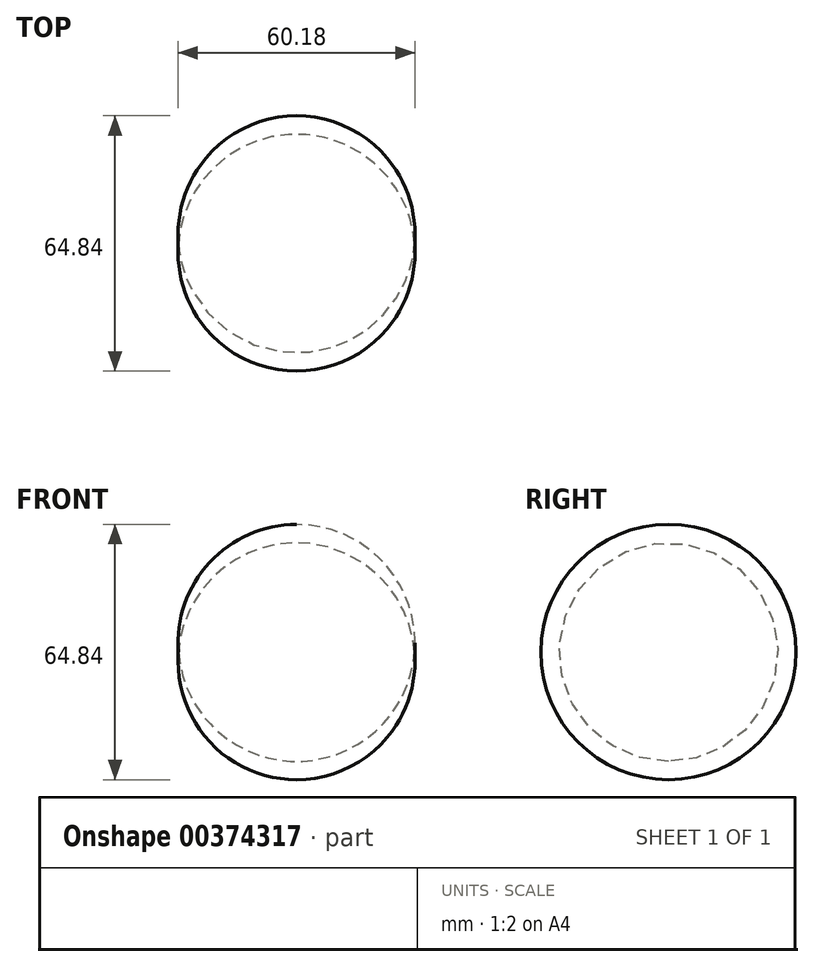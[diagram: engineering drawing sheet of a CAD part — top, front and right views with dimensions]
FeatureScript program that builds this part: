
annotation { "Feature Type Name" : "Feature", "Feature Type Description" : "" }
export const myFeature = defineFeature(function(context is Context, id is Id, definition is map)
    precondition{}
    {
        {
            var Q0;
            Q0=qCreatedBy(makeId("Front.planeOp"),FACE);
            var sketch = newSketch(context, id + "F0", { "sketchPlane" : qUnion([Q0])});
            skLineSegment(sketch, "E0", {"start": v(-30, 0) * mm, "end": v(30, 0) * mm});
            skArc(sketch, "E1", {"start": v(30, 0) * mm, "mid": v(0, 32.42) * mm, "end": v(-30, 0) * mm});
            skSolve(sketch);
        }
        {
            var Q0;
            Q0=makeQuery(id+"F0.imprint","IMPRINT",FACE,{"disambiguationData":[TD([[makeQuery(id+"F0.imprint","IMPRINT",EDGE,{"derivedFrom":sQuery(id+"F0.wireOp",EDGE,"E0")}),1.0]])]});
            var Q1;
            Q1=sQuery(id+"F0.wireOp",EDGE,"E0");
            revolve(context, id + "F1", {"entities" : qUnion([Q0]), "axis" : qUnion([Q1]), "revolveType" : RevolveType.FULL});
        }
    });
